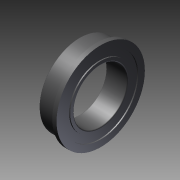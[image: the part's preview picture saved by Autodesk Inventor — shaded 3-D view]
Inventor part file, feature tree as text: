
AUTODESK INVENTOR PART (.ipt)
format: ipt  version: 2011 SP1 (Build 150282100, 282)  size: 161,792 bytes
history: native  units: mm
features: other x7, revolve x1, sketch x1
ambient origin geometry x8: Origin, YZ Plane, XZ Plane, XY Plane, X Axis, Y Axis, Z Axis, Center Point
bodies: Solid1 (feature_tree)
feature tree (9):
  revolve  "Revolution1"  [1 undecoded]
  other  "to_housing_XY"
  other  "to_housing_YZ"
  other  "to_housing_ZX"
  other  "to_housing_X"
  other  "to_housing_Y"
  other  "to_housing_Z"
  other  "to_housing_Center"
  sketch  "Sketch_1"  dims[d0=360.0deg d1=0.0mm]
note: 1 required parameter value undecoded (feature->parameter linkage not recoverable at this tier; creation-order binding heuristic only, values carry confidence <= 0.55)
